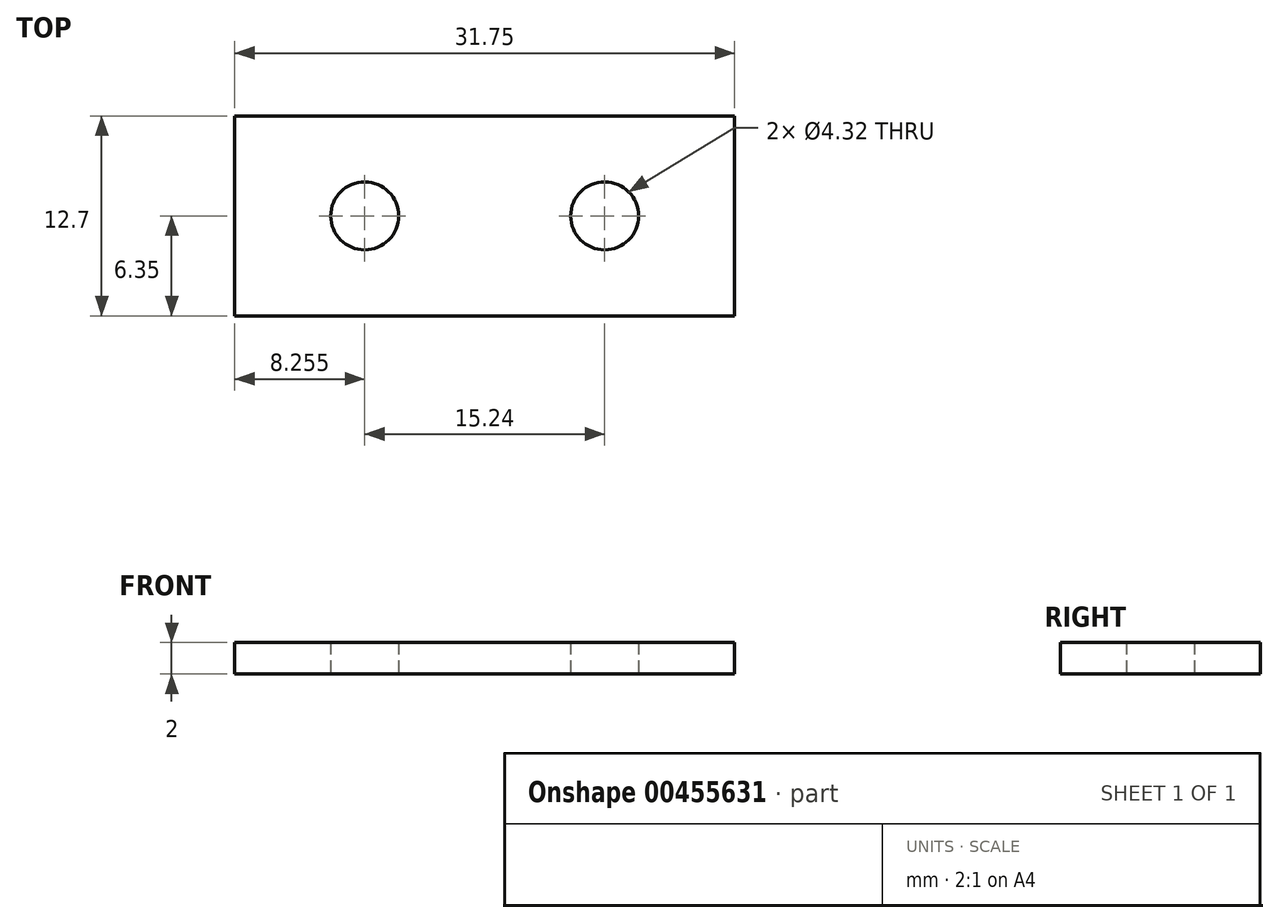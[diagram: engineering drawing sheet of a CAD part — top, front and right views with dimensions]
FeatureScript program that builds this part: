
annotation { "Feature Type Name" : "Feature", "Feature Type Description" : "" }
export const myFeature = defineFeature(function(context is Context, id is Id, definition is map)
    precondition{}
    {
        {
            var Q0;
            Q0=qCreatedBy(makeId("Top.planeOp"),FACE);
            var sketch = newSketch(context, id + "F0", { "sketchPlane" : qUnion([Q0])});
            skLineSegment(sketch, "E0.bottom", {"start": v(0, 0) * mm, "end": v(31.75, 0) * mm});
            skLineSegment(sketch, "E0.top", {"start": v(0, 12.7) * mm, "end": v(31.75, 12.7) * mm});
            skLineSegment(sketch, "E0.left", {"start": v(0, 0) * mm, "end": v(0, 12.7) * mm});
            skLineSegment(sketch, "E0.right", {"start": v(31.75, 0) * mm, "end": v(31.75, 12.7) * mm});
            skLineSegment(sketch, "E1", {"start": v(31.75, 6.35) * mm, "end": v(0, 6.35) * mm, "construction": true});
            skCircle(sketch, "E2", {"center": v(23.5, 6.35) * mm, "radius": 2.16 * mm});
            skLineSegment(sketch, "E3", {"start": v(15.88, 0) * mm, "end": v(15.88, 12.7) * mm, "construction": true});
            skCircle(sketch, "E4.MirrorC", {"center": v(8.26, 6.35) * mm, "radius": 2.16 * mm});
            skSolve(sketch);
        }
        {
            var Q0;
            Q0=makeQuery(id+"F0.imprint","IMPRINT",FACE,{"disambiguationData":[TD([[makeQuery(id+"F0.imprint","IMPRINT",EDGE,{"derivedFrom":sQuery(id+"F0.wireOp",EDGE,"E0.bottom")}),1.0]])]});
            extrude(context, id + "F1", {"entities" : qUnion([Q0]), "depth" : 2 * mm});
        }
    });
